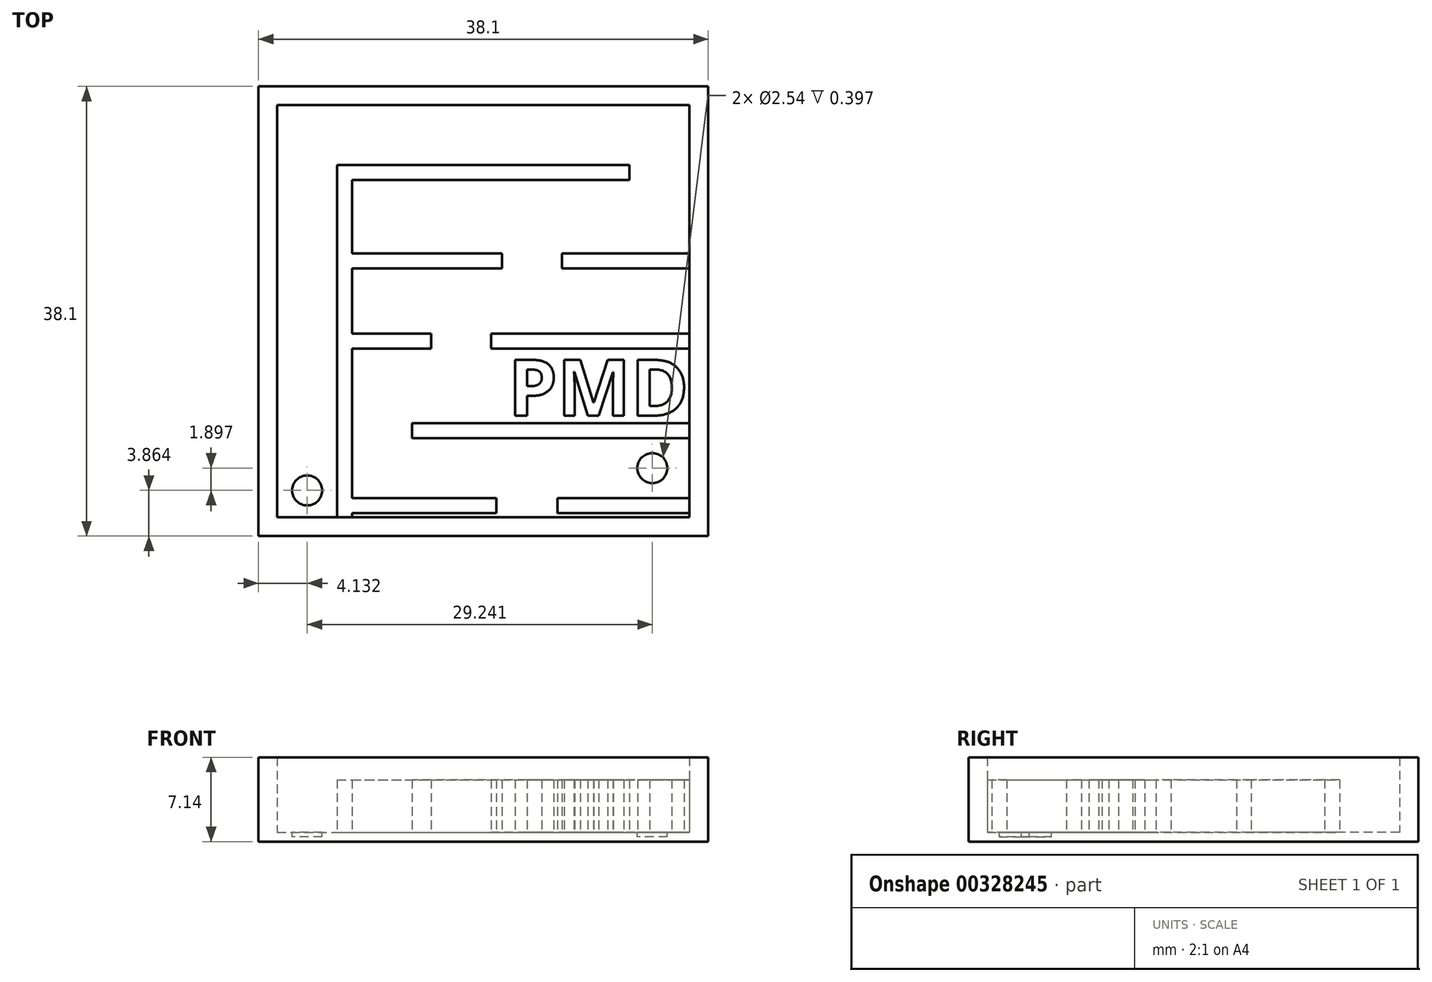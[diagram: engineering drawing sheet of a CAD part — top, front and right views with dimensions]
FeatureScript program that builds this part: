
annotation { "Feature Type Name" : "Feature", "Feature Type Description" : "" }
export const myFeature = defineFeature(function(context is Context, id is Id, definition is map)
    precondition{}
    {
        {
            var Q0;
            Q0=qCreatedBy(makeId("Top.planeOp"),FACE);
            var sketch = newSketch(context, id + "F0", { "sketchPlane" : qUnion([Q0])});
            skLineSegment(sketch, "E0.bottom", {"start": v(-11.85, 7.42) * mm, "end": v(26.25, 7.42) * mm});
            skLineSegment(sketch, "E0.top", {"start": v(-11.85, -30.68) * mm, "end": v(26.25, -30.68) * mm});
            skLineSegment(sketch, "E0.left", {"start": v(-11.85, 7.42) * mm, "end": v(-11.85, -30.68) * mm});
            skLineSegment(sketch, "E0.right", {"start": v(26.25, 7.42) * mm, "end": v(26.25, -30.68) * mm});
            skSolve(sketch);
        }
        {
            var Q0;
            Q0=makeQuery(id+"F0.imprint","IMPRINT",FACE,{"disambiguationData":[TD([[makeQuery(id+"F0.imprint","IMPRINT",EDGE,{"derivedFrom":sQuery(id+"F0.wireOp",EDGE,"E0.bottom")}),-1.0]])]});
            extrude(context, id + "F1", {"entities" : qUnion([Q0]), "depth" : 0.8 * mm});
        }
        {
            var Q0;
            Q0=makeQuery(id+"F1.opExtrude","CAP_FACE",FACE,{"disambiguationData":[OSD([sQuery(id+"F0.wireOp",EDGE,"E0.bottom"),sQuery(id+"F0.wireOp",EDGE,"E0.top"),sQuery(id+"F0.wireOp",EDGE,"E0.left"),sQuery(id+"F0.wireOp",EDGE,"E0.right")])],"isStart":false});
            var sketch = newSketch(context, id + "F2", { "sketchPlane" : qUnion([Q0])});
            skLineSegment(sketch, "E1.0", {"start": v(-10.26, 5.83) * mm, "end": v(24.66, 5.83) * mm});
            skLineSegment(sketch, "E1.1", {"start": v(-10.26, 5.83) * mm, "end": v(-10.26, -29.1) * mm});
            skLineSegment(sketch, "E1.2", {"start": v(-10.26, -29.1) * mm, "end": v(24.66, -29.1) * mm});
            skLineSegment(sketch, "E1.3", {"start": v(24.66, 5.83) * mm, "end": v(24.66, -29.1) * mm});
            skSolve(sketch);
        }
        {
            var Q0;
            Q0=makeQuery(id+"F2.imprint","IMPRINT",FACE,{"disambiguationData":[TD([[makeQuery(id+"F2.imprint","IMPRINT",EDGE,{"derivedFrom":sQuery(id+"F2.wireOp",EDGE,"E1.0")}),1.0]])]});
            extrude(context, id + "F3", {"entities" : qUnion([Q0]), "operationType" : NewBodyOperationType.ADD, "depth" : 6.35 * mm});
        }
        {
            var Q0;
            Q0=makeQuery(id+"F1.opExtrude","CAP_FACE",FACE,{"disambiguationData":[OSD([sQuery(id+"F0.wireOp",EDGE,"E0.bottom"),sQuery(id+"F0.wireOp",EDGE,"E0.top"),sQuery(id+"F0.wireOp",EDGE,"E0.left"),sQuery(id+"F0.wireOp",EDGE,"E0.right")])],"isStart":false});
            var sketch = newSketch(context, id + "F4", { "sketchPlane" : qUnion([Q0])});
            skLineSegment(sketch, "E2.left", {"start": v(-5.18, -29.1) * mm, "end": v(-5.18, 0.75) * mm});
            skCircle(sketch, "E3", {"center": v(-7.72, -26.82) * mm, "radius": 1.27 * mm});
            skLineSegment(sketch, "E4", {"start": v(-5.18, -29.1) * mm, "end": v(-3.91, -29.1) * mm});
            skLineSegment(sketch, "E5", {"start": v(-3.91, -0.52) * mm, "end": v(19.58, -0.52) * mm});
            skLineSegment(sketch, "E6", {"start": v(19.58, 0.75) * mm, "end": v(19.58, -0.52) * mm});
            skLineSegment(sketch, "E7", {"start": v(-5.18, 0.75) * mm, "end": v(19.58, 0.75) * mm});
            skLineSegment(sketch, "E8.bottom", {"start": v(24.66, -8) * mm, "end": v(13.87, -8) * mm});
            skLineSegment(sketch, "E8.top", {"start": v(24.66, -6.72) * mm, "end": v(13.87, -6.72) * mm});
            skLineSegment(sketch, "E8.left", {"start": v(24.66, -6.72) * mm, "end": v(24.66, -8) * mm});
            skLineSegment(sketch, "E8.right", {"start": v(13.87, -6.72) * mm, "end": v(13.87, -8) * mm});
            skLineSegment(sketch, "E9", {"start": v(-3.91, -0.52) * mm, "end": v(-3.91, -6.72) * mm});
            skPoint(sketch, "E10.firstSnap0", {"position": v(-3.91, -14.8) * mm});
            skLineSegment(sketch, "E10.bottom", {"start": v(-3.91, -6.72) * mm, "end": v(8.79, -6.72) * mm});
            skLineSegment(sketch, "E10.top", {"start": v(-3.91, -8) * mm, "end": v(8.79, -8) * mm});
            skLineSegment(sketch, "E10.right", {"start": v(8.79, -6.72) * mm, "end": v(8.79, -8) * mm});
            skLineSegment(sketch, "E11.bottom", {"start": v(-3.91, -14.8) * mm, "end": v(2.79, -14.8) * mm});
            skLineSegment(sketch, "E11.top", {"start": v(-3.91, -13.53) * mm, "end": v(2.79, -13.53) * mm});
            skLineSegment(sketch, "E11.right", {"start": v(2.79, -14.8) * mm, "end": v(2.79, -13.53) * mm});
            skLineSegment(sketch, "E12.bottom", {"start": v(24.66, -13.53) * mm, "end": v(7.87, -13.53) * mm});
            skLineSegment(sketch, "E12.top", {"start": v(24.66, -14.8) * mm, "end": v(7.87, -14.8) * mm});
            skLineSegment(sketch, "E12.left", {"start": v(24.66, -13.53) * mm, "end": v(24.66, -14.8) * mm});
            skLineSegment(sketch, "E12.right", {"start": v(7.87, -13.53) * mm, "end": v(7.87, -14.8) * mm});
            skLineSegment(sketch, "E13.trimOffspring", {"start": v(-3.91, -8) * mm, "end": v(-3.91, -13.53) * mm});
            skText(sketch, "E14", { "text": "PMD", "fontName": "OpenSans-Bold.ttf"});
            skLineSegment(sketch, "E15", {"start": v(-3.91, -29.1) * mm, "end": v(-3.91, -14.8) * mm});
            skLineSegment(sketch, "E16.bottom", {"start": v(24.66, -21.11) * mm, "end": v(1.17, -21.11) * mm});
            skLineSegment(sketch, "E16.right", {"start": v(1.17, -21.11) * mm, "end": v(1.17, -22.38) * mm});
            skLineSegment(sketch, "E17", {"start": v(1.17, -22.38) * mm, "end": v(24.66, -22.38) * mm});
            skLineSegment(sketch, "E18.bottom", {"start": v(-3.91, -27.45) * mm, "end": v(8.3, -27.45) * mm});
            skLineSegment(sketch, "E18.top", {"start": v(-3.91, -28.72) * mm, "end": v(8.3, -28.72) * mm});
            skLineSegment(sketch, "E18.left", {"start": v(-3.91, -27.45) * mm, "end": v(-3.91, -28.72) * mm});
            skLineSegment(sketch, "E18.right", {"start": v(8.3, -27.45) * mm, "end": v(8.3, -28.72) * mm});
            skLineSegment(sketch, "E19.bottom", {"start": v(13.49, -27.45) * mm, "end": v(24.66, -27.45) * mm});
            skLineSegment(sketch, "E19.top", {"start": v(13.49, -28.72) * mm, "end": v(24.66, -28.72) * mm});
            skLineSegment(sketch, "E19.left", {"start": v(13.49, -27.45) * mm, "end": v(13.49, -28.72) * mm});
            skLineSegment(sketch, "E19.right", {"start": v(24.66, -27.45) * mm, "end": v(24.66, -28.72) * mm});
            skCircle(sketch, "E20", {"center": v(21.52, -24.92) * mm, "radius": 1.27 * mm});
            const initialGuessF4  = {"E14": [0.00931, -0.02048, 1, 0, 0.00476]};
            skSetInitialGuess(sketch, initialGuessF4);
            skSolve(sketch);
        }
        {
            var Q0;
            Q0=makeQuery(id+"F4.imprint","IMPRINT",FACE,{"disambiguationData":[TD([[makeQuery(id+"F4.imprint","IMPRINT",EDGE,{"derivedFrom":sQuery(id+"F4.wireOp",EDGE,"E3")}),1.0]])]});
            var Q1;
            Q1=makeQuery(id+"F4.imprint","IMPRINT",FACE,{"disambiguationData":[TD([[makeQuery(id+"F4.imprint","IMPRINT",EDGE,{"derivedFrom":sQuery(id+"F4.wireOp",EDGE,"E20")}),1.0]])]});
            extrude(context, id + "F5", {"entities" : qUnion([Q0, Q1]), "operationType" : NewBodyOperationType.REMOVE, "oppositeDirection" : true, "depth" : 0.4 * mm});
        }
        {
            var Q0;
            Q0=makeQuery(id+"F4.imprint","IMPRINT",FACE,{"disambiguationData":[TD([[makeQuery(id+"F4.imprint","IMPRINT",EDGE,{"derivedFrom":sQuery(id+"F4.wireOp",EDGE,"E2.left")}),-1.0]])]});
            var Q1;
            Q1=makeQuery(id+"F4.imprint","IMPRINT",FACE,{"disambiguationData":[TD([[makeQuery(id+"F4.imprint","IMPRINT",EDGE,{"derivedFrom":sQuery(id+"F4.wireOp",EDGE,"E8.bottom")}),-1.0]])]});
            var Q2;
            Q2=makeQuery(id+"F4.imprint","IMPRINT",FACE,{"disambiguationData":[TD([[makeQuery(id+"F4.imprint","IMPRINT",EDGE,{"derivedFrom":sQuery(id+"F4.wireOp",EDGE,"E12.bottom")}),1.0]])]});
            var Q3;
            {var subQ0=sQuery(id+"F4.wireOp",EDGE,"E16.bottom");Q3=makeQuery(id+"F4.imprint","IMPRINT",FACE,{"disambiguationData":[TD([[makeQuery(id+"F4.imprint","IMPRINT",EDGE,{"derivedFrom":subQ0}),1.0]])]});}
            var Q4;
            Q4=makeQuery(id+"F4.imprint","IMPRINT",FACE,{"disambiguationData":[TD([[makeQuery(id+"F4.imprint","IMPRINT",EDGE,{"derivedFrom":sQuery(id+"F4.wireOp",EDGE,"E18.bottom")}),-1.0]])]});
            var Q5;
            Q5=makeQuery(id+"F4.imprint","IMPRINT",FACE,{"disambiguationData":[TD([[makeQuery(id+"F4.imprint","IMPRINT",EDGE,{"derivedFrom":sQuery(id+"F4.wireOp",EDGE,"E19.bottom")}),-1.0]])]});
            extrude(context, id + "F6", {"entities" : qUnion([Q0, Q1, Q2, Q3, Q4, Q5]), "operationType" : NewBodyOperationType.ADD, "depth" : 4.44 * mm});
        }
        {
            var Q0;
            Q0=makeQuery(id+"F4.imprint","IMPRINT",FACE,{"disambiguationData":[TD([[makeQuery(id+"F4.imprint","IMPRINT",EDGE,{"derivedFrom":sQuery(id+"F4.wireOp",EDGE,"E14.sketch_text.stroke-0")}),-1.0]])]});
            var Q1;
            Q1=makeQuery(id+"F4.imprint","IMPRINT",FACE,{"disambiguationData":[TD([[makeQuery(id+"F4.imprint","IMPRINT",EDGE,{"derivedFrom":sQuery(id+"F4.wireOp",EDGE,"E14.sketch_text.stroke-16")}),-1.0]])]});
            var Q2;
            Q2=makeQuery(id+"F4.imprint","IMPRINT",FACE,{"disambiguationData":[TD([[makeQuery(id+"F4.imprint","IMPRINT",EDGE,{"derivedFrom":sQuery(id+"F4.wireOp",EDGE,"E14.sketch_text.stroke-35")}),-1.0]])]});
            extrude(context, id + "F7", {"entities" : qUnion([Q0, Q1, Q2]), "operationType" : NewBodyOperationType.ADD, "depth" : 4.44 * mm});
        }
    });
